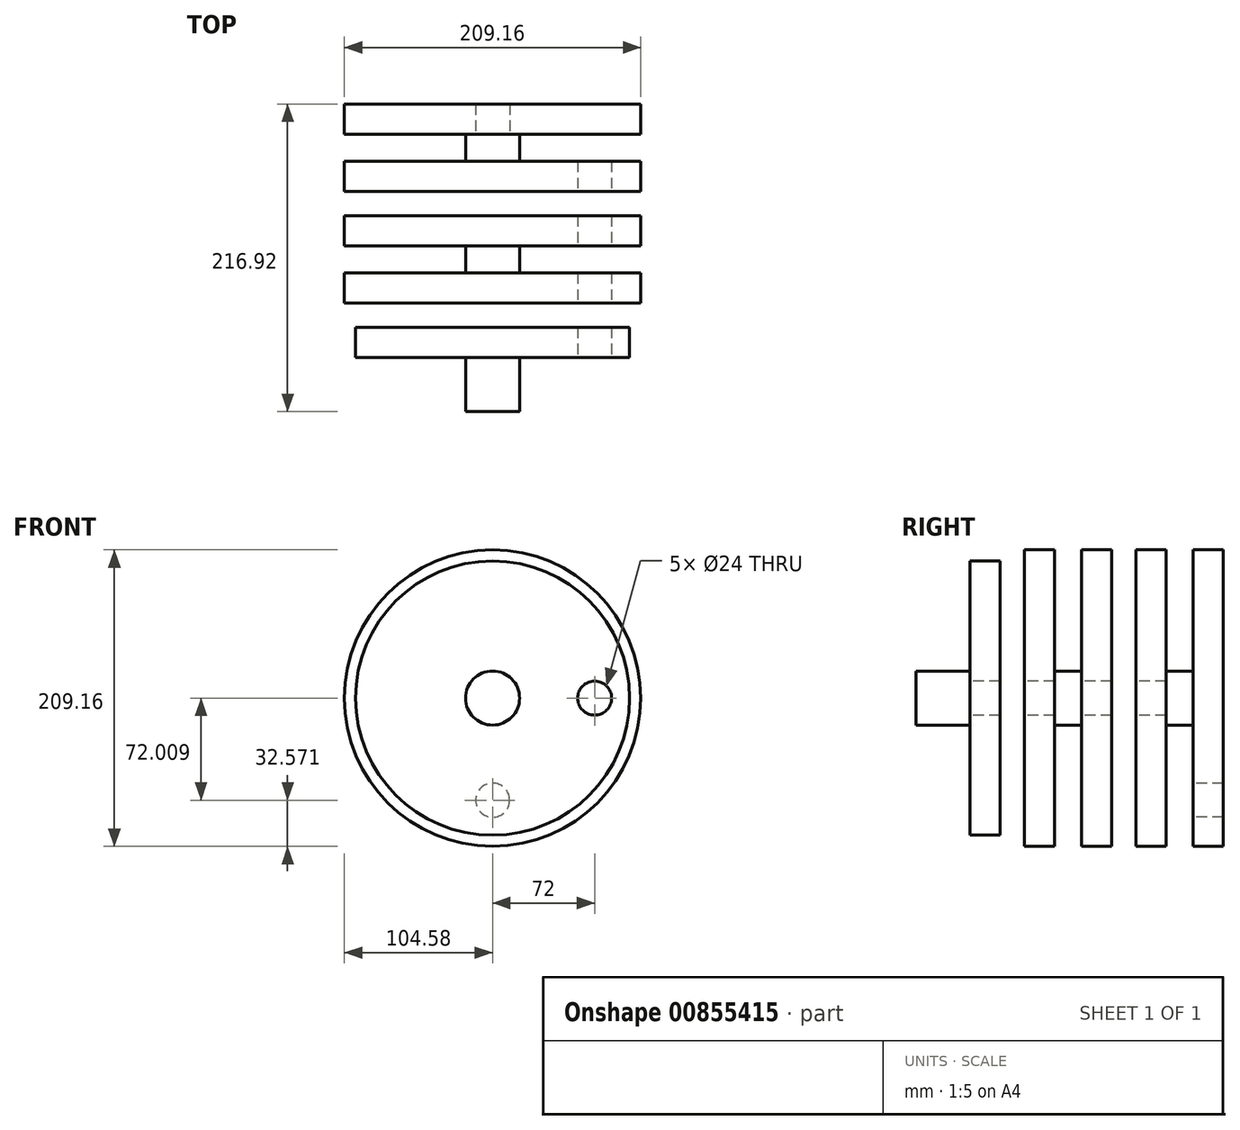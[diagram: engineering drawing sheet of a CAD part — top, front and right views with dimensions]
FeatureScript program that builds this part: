
annotation { "Feature Type Name" : "Feature", "Feature Type Description" : "" }
export const myFeature = defineFeature(function(context is Context, id is Id, definition is map)
    precondition{}
    {
        {
            var Q0;
            Q0=qCreatedBy(makeId("Front.planeOp"),FACE);
            var sketch = newSketch(context, id + "F0", { "sketchPlane" : qUnion([Q0])});
            skCircle(sketch, "E0", {"center": v(0, 0) * mm, "radius": 96.7 * mm});
            skCircle(sketch, "E1", {"center": v(72, 0) * mm, "radius": 12 * mm});
            skPoint(sketch, "E2", {"position": v(84, 0) * mm});
            skPoint(sketch, "E3", {"position": v(96.7, 0) * mm});
            skSolve(sketch);
        }
        {
            var Q0;
            Q0=makeQuery(id+"F0.imprint","IMPRINT",FACE,{"disambiguationData":[TD([[makeQuery(id+"F0.imprint","IMPRINT",EDGE,{"derivedFrom":sQuery(id+"F0.wireOp",EDGE,"E0")}),1.0]])]});
            extrude(context, id + "F1", {"entities" : qUnion([Q0]), "oppositeDirection" : true, "depth" : 21.34 * mm, "offsetDistance" : 25.4 * mm});
        }
        {
            var Q0;
            Q0=makeQuery(id+"F1.opExtrude","CAP_FACE",FACE,{"disambiguationData":[OSD([sQuery(id+"F0.wireOp",EDGE,"E0"),sQuery(id+"F0.wireOp",EDGE,"E1")])],"isStart":true});
            var sketch = newSketch(context, id + "F2", { "sketchPlane" : qUnion([Q0])});
            skCircle(sketch, "E4", {"center": v(0, 0) * mm, "radius": 19.05 * mm});
            skSolve(sketch);
        }
        {
            var Q0;
            Q0=makeQuery(id+"F2.imprint","IMPRINT",FACE,{"disambiguationData":[TD([[makeQuery(id+"F2.imprint","IMPRINT",EDGE,{"derivedFrom":sQuery(id+"F2.wireOp",EDGE,"E4")}),1.0]])]});
            extrude(context, id + "F3", {"entities" : qUnion([Q0]), "operationType" : NewBodyOperationType.ADD, "depth" : 38.1 * mm, "offsetDistance" : 25.4 * mm});
        }
        {
            var Q0;
            Q0=makeQuery(id+"F1.opExtrude","CAP_FACE",FACE,{"disambiguationData":[OSD([sQuery(id+"F0.wireOp",EDGE,"E0"),sQuery(id+"F0.wireOp",EDGE,"E1")])],"isStart":false});
            cPlane(context, id + "F4", {"entities" : qUnion([Q0]), "cplaneType" : CPlaneType.OFFSET, "offset" : 17.02 * mm, "width" : 152.4 * mm, "height" : 152.4 * mm});
        }
        {
            var Q0;
            Q0=qCreatedBy(id+"F4.planeOp",FACE);
            var sketch = newSketch(context, id + "F5", { "sketchPlane" : qUnion([Q0])});
            skCircle(sketch, "E5", {"center": v(0, 0) * mm, "radius": 104.58 * mm});
            skCircle(sketch, "E6", {"center": v(-72, 0) * mm, "radius": 12 * mm});
            skPoint(sketch, "E7", {"position": v(-84, 0) * mm});
            skPoint(sketch, "E8", {"position": v(-104.58, 0) * mm});
            skCircle(sketch, "E9", {"center": v(0, 0) * mm, "radius": 19.05 * mm});
            skSolve(sketch);
        }
        {
            var Q0;
            Q0=makeQuery(id+"F5.imprint","IMPRINT",FACE,{"disambiguationData":[TD([[makeQuery(id+"F5.imprint","IMPRINT",EDGE,{"derivedFrom":sQuery(id+"F5.wireOp",EDGE,"E5")}),1.0]])]});
            extrude(context, id + "F6", {"entities" : qUnion([Q0]), "depth" : 21.34 * mm, "offsetDistance" : 25.4 * mm});
        }
        {
            var Q0;
            Q0=makeQuery(id+"F5.imprint","IMPRINT",FACE,{"disambiguationData":[TD([[makeQuery(id+"F5.imprint","IMPRINT",EDGE,{"derivedFrom":sQuery(id+"F5.wireOp",EDGE,"E9")}),1.0]])]});
            extrude(context, id + "F7", {"entities" : qUnion([Q0]), "operationType" : NewBodyOperationType.ADD, "depth" : 61.72 * mm, "offsetDistance" : 25.4 * mm});
        }
        {
            var Q0;
            Q0=makeQuery(id+"F6.opExtrude","CAP_FACE",FACE,{"disambiguationData":[OSD([sQuery(id+"F5.wireOp",EDGE,"E5"),sQuery(id+"F5.wireOp",EDGE,"E6"),sQuery(id+"F5.wireOp",EDGE,"E9")])],"isStart":false});
            cPlane(context, id + "F8", {"entities" : qUnion([Q0]), "cplaneType" : CPlaneType.OFFSET, "offset" : 19.05 * mm, "width" : 152.4 * mm, "height" : 152.4 * mm});
        }
        {
            var Q0;
            Q0=qCreatedBy(id+"F8.planeOp",FACE);
            var sketch = newSketch(context, id + "F9", { "sketchPlane" : qUnion([Q0])});
            skCircle(sketch, "E10", {"center": v(0, 0) * mm, "radius": 104.58 * mm});
            skCircle(sketch, "E11", {"center": v(-72, 0) * mm, "radius": 12 * mm});
            skPoint(sketch, "E12", {"position": v(-84, 0) * mm});
            skPoint(sketch, "E13", {"position": v(-104.58, 0) * mm});
            skSolve(sketch);
        }
        {
            var Q0;
            Q0=makeQuery(id+"F9.imprint","IMPRINT",FACE,{"disambiguationData":[TD([[makeQuery(id+"F9.imprint","IMPRINT",EDGE,{"derivedFrom":sQuery(id+"F9.wireOp",EDGE,"E10")}),1.0]])]});
            extrude(context, id + "F10", {"entities" : qUnion([Q0]), "operationType" : NewBodyOperationType.ADD, "depth" : 21.34 * mm, "offsetDistance" : 25.4 * mm});
        }
        {
            var Q0;
            Q0=makeQuery(id+"F10.boolean.opBoolean","MERGE",FACE,{"derivedFrom":[makeQuery(id+"F7.opExtrude","CAP_FACE",FACE,{"disambiguationData":[OSD([sQuery(id+"F5.wireOp",EDGE,"E9")])],"isStart":false}),makeQuery(id+"F10.opExtrude","CAP_FACE",FACE,{"disambiguationData":[OSD([sQuery(id+"F9.wireOp",EDGE,"E10"),sQuery(id+"F9.wireOp",EDGE,"E11")])],"isStart":false})]});
            cPlane(context, id + "F11", {"entities" : qUnion([Q0]), "cplaneType" : CPlaneType.OFFSET, "offset" : 17.02 * mm, "width" : 152.4 * mm, "height" : 152.4 * mm});
        }
        {
            var Q0;
            Q0=qCreatedBy(id+"F11.planeOp",FACE);
            var sketch = newSketch(context, id + "F12", { "sketchPlane" : qUnion([Q0])});
            skCircle(sketch, "E14", {"center": v(0, 0) * mm, "radius": 104.58 * mm});
            skCircle(sketch, "E15", {"center": v(-72, 0) * mm, "radius": 12 * mm});
            skPoint(sketch, "E16", {"position": v(-84, 0) * mm});
            skPoint(sketch, "E17", {"position": v(-104.58, 0) * mm});
            skCircle(sketch, "E18", {"center": v(0, 0) * mm, "radius": 19.05 * mm});
            skSolve(sketch);
        }
        {
            var Q0;
            Q0=makeQuery(id+"F12.imprint","IMPRINT",FACE,{"disambiguationData":[TD([[makeQuery(id+"F12.imprint","IMPRINT",EDGE,{"derivedFrom":sQuery(id+"F12.wireOp",EDGE,"E14")}),1.0]])]});
            extrude(context, id + "F13", {"entities" : qUnion([Q0]), "depth" : 21.34 * mm, "offsetDistance" : 25.4 * mm});
        }
        {
            var Q0;
            Q0=makeQuery(id+"F12.imprint","IMPRINT",FACE,{"disambiguationData":[TD([[makeQuery(id+"F12.imprint","IMPRINT",EDGE,{"derivedFrom":sQuery(id+"F12.wireOp",EDGE,"E18")}),1.0]])]});
            extrude(context, id + "F14", {"entities" : qUnion([Q0]), "operationType" : NewBodyOperationType.ADD, "depth" : 61.72 * mm, "offsetDistance" : 25.4 * mm});
        }
        {
            var Q0;
            Q0=makeQuery(id+"F13.opExtrude","CAP_FACE",FACE,{"disambiguationData":[OSD([sQuery(id+"F12.wireOp",EDGE,"E14"),sQuery(id+"F12.wireOp",EDGE,"E15"),sQuery(id+"F12.wireOp",EDGE,"E18")])],"isStart":false});
            cPlane(context, id + "F15", {"entities" : qUnion([Q0]), "cplaneType" : CPlaneType.OFFSET, "offset" : 19.05 * mm, "width" : 152.4 * mm, "height" : 152.4 * mm});
        }
        {
            var Q0;
            Q0=qCreatedBy(id+"F15.planeOp",FACE);
            var sketch = newSketch(context, id + "F16", { "sketchPlane" : qUnion([Q0])});
            skCircle(sketch, "E19", {"center": v(0, 0) * mm, "radius": 104.58 * mm});
            skCircle(sketch, "E20", {"center": v(0, -72) * mm, "radius": 12 * mm});
            skPoint(sketch, "E21", {"position": v(0, -84.01) * mm});
            skPoint(sketch, "E22", {"position": v(0, -104.58) * mm});
            skSolve(sketch);
        }
        {
            var Q0;
            Q0=makeQuery(id+"F16.imprint","IMPRINT",FACE,{"disambiguationData":[TD([[makeQuery(id+"F16.imprint","IMPRINT",EDGE,{"derivedFrom":sQuery(id+"F16.wireOp",EDGE,"E19")}),1.0]])]});
            extrude(context, id + "F17", {"entities" : qUnion([Q0]), "operationType" : NewBodyOperationType.ADD, "depth" : 21.34 * mm, "offsetDistance" : 25.4 * mm});
        }
    });
